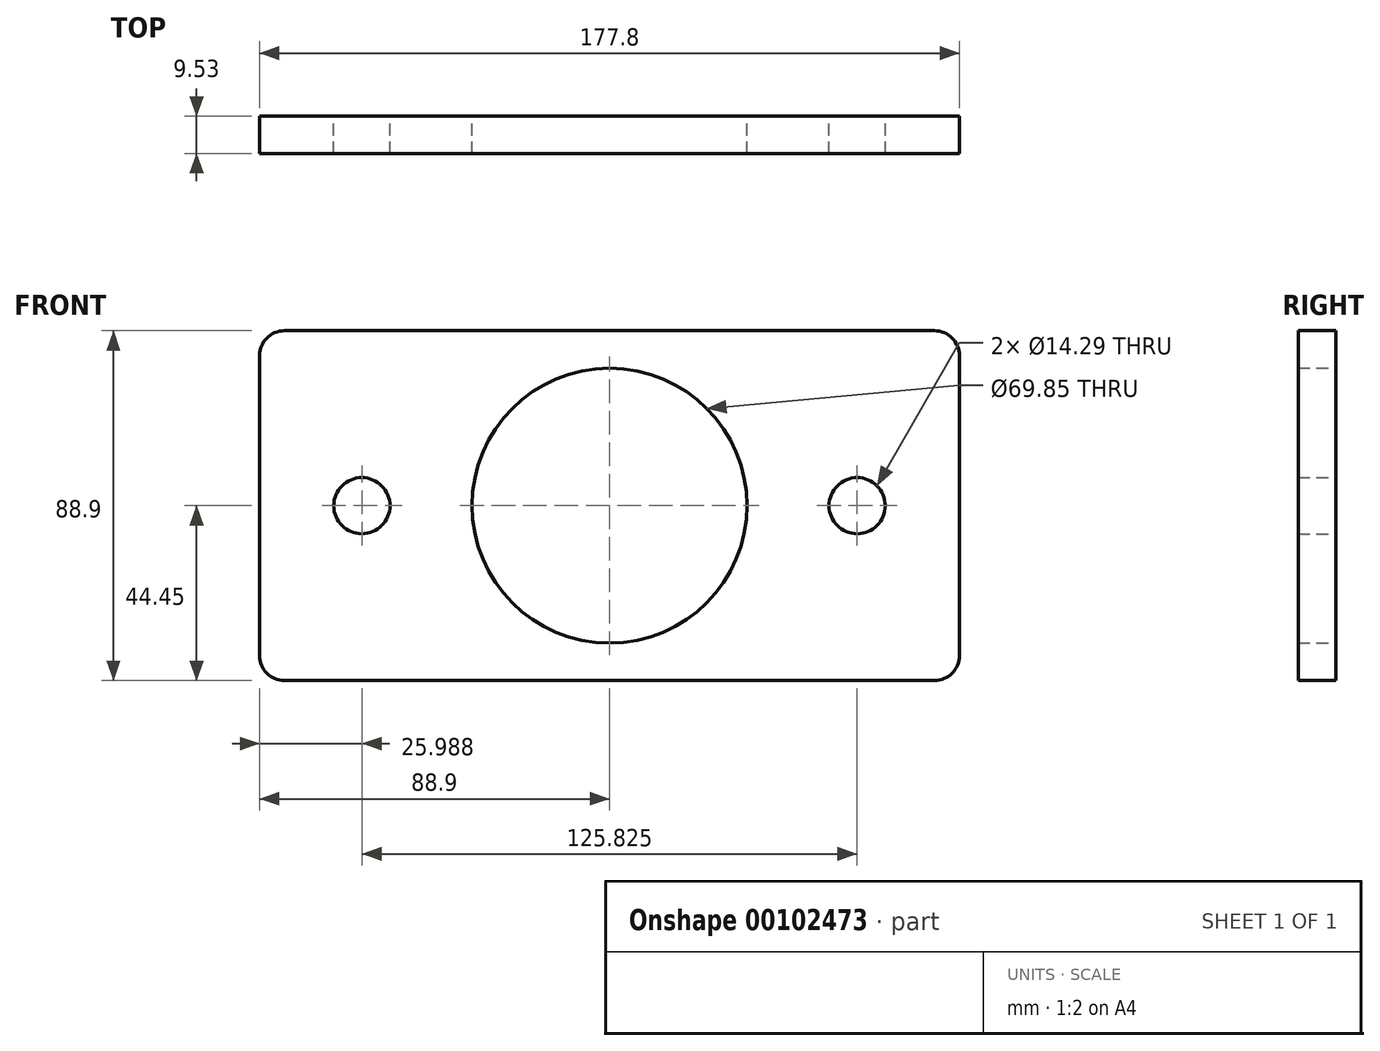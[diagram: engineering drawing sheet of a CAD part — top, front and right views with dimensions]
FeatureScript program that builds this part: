
annotation { "Feature Type Name" : "Feature", "Feature Type Description" : "" }
export const myFeature = defineFeature(function(context is Context, id is Id, definition is map)
    precondition{}
    {
        {
            var Q0;
            Q0=qCreatedBy(makeId("Front.planeOp"),FACE);
            var sketch = newSketch(context, id + "F0", { "sketchPlane" : qUnion([Q0])});
            skCircle(sketch, "E0", {"center": v(-62.91, 0) * mm, "radius": 7.14 * mm});
            skCircle(sketch, "E1", {"center": v(62.91, 0) * mm, "radius": 7.14 * mm});
            skLineSegment(sketch, "E2", {"start": v(82.55, 44.45) * mm, "end": v(-82.55, 44.45) * mm});
            skArc(sketch, "E3", {"start": v(-82.55, 44.45) * mm, "mid": v(-87.04, 42.6) * mm, "end": v(-88.9, 38.1) * mm});
            skLineSegment(sketch, "E4", {"start": v(-88.9, 38.1) * mm, "end": v(-88.9, -38.1) * mm});
            skArc(sketch, "E5", {"start": v(-88.9, -38.1) * mm, "mid": v(-87.04, -42.6) * mm, "end": v(-82.55, -44.45) * mm});
            skLineSegment(sketch, "E6", {"start": v(-82.55, -44.45) * mm, "end": v(82.55, -44.45) * mm});
            skArc(sketch, "E7", {"start": v(82.55, -44.45) * mm, "mid": v(87.04, -42.6) * mm, "end": v(88.9, -38.1) * mm});
            skLineSegment(sketch, "E8", {"start": v(88.9, -38.1) * mm, "end": v(88.9, 38.1) * mm});
            skArc(sketch, "E9", {"start": v(88.9, 38.1) * mm, "mid": v(87.04, 42.6) * mm, "end": v(82.55, 44.45) * mm});
            skCircle(sketch, "E10", {"center": v(0, 0) * mm, "radius": 34.93 * mm});
            skSolve(sketch);
        }
        {
            var Q0;
            Q0 = qSketchRegion(id + "F0", true);
            extrude(context, id + "F1", {"entities" : qUnion([Q0]), "depth" : 9.52 * mm});
        }
    });
